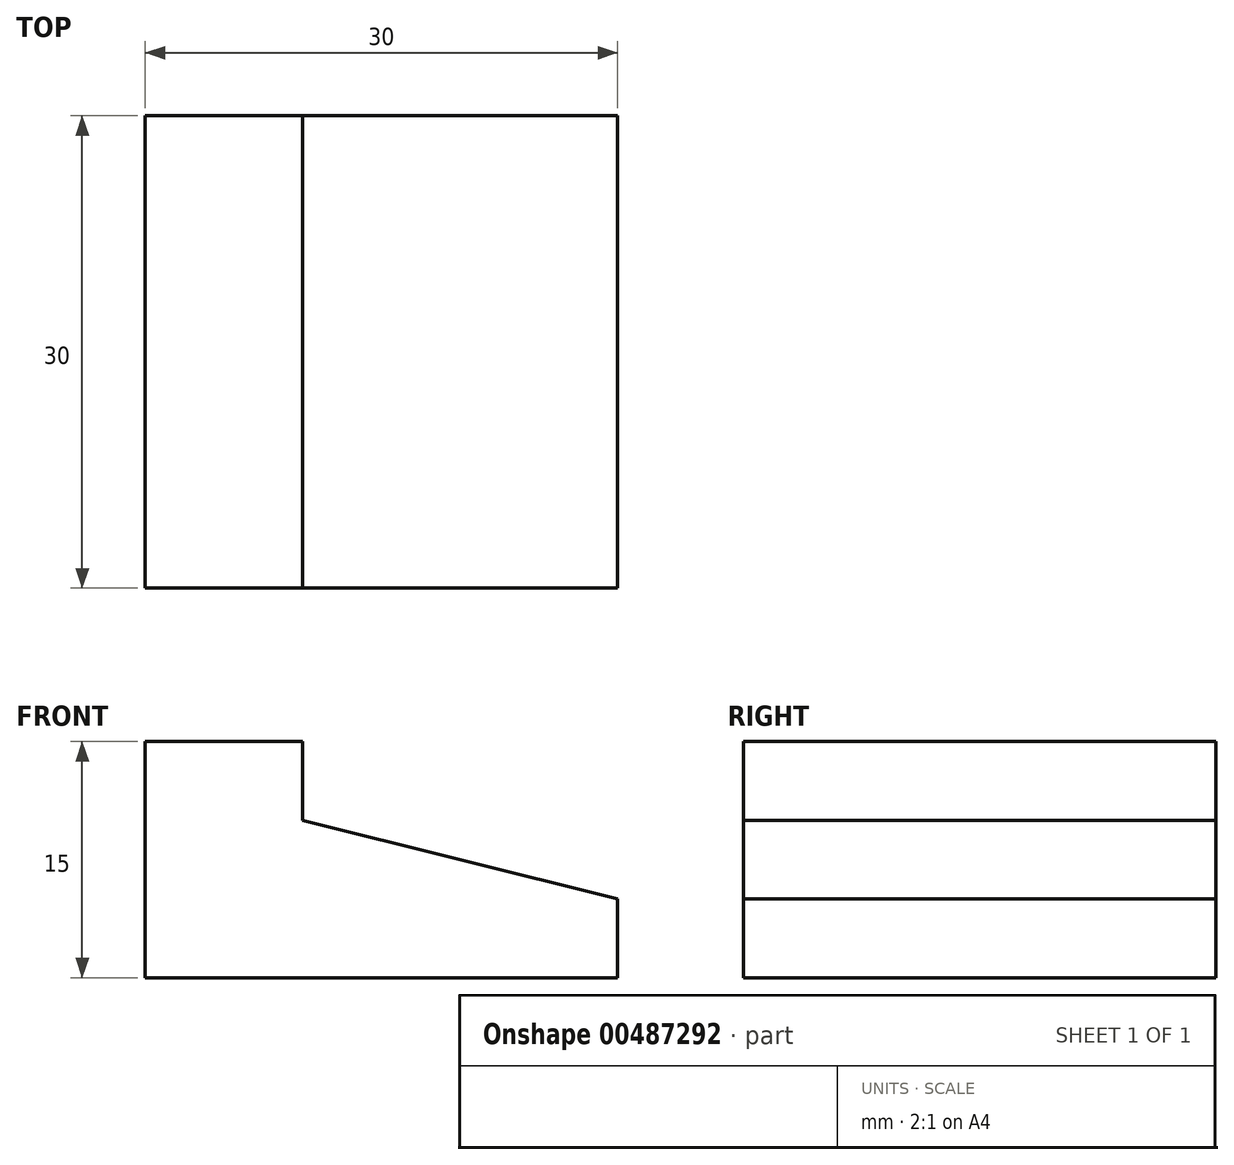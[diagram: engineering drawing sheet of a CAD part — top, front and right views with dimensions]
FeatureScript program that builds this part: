
annotation { "Feature Type Name" : "Feature", "Feature Type Description" : "" }
export const myFeature = defineFeature(function(context is Context, id is Id, definition is map)
    precondition{}
    {
        {
            var Q0;
            Q0=qCreatedBy(makeId("Top.planeOp"),FACE);
            var sketch = newSketch(context, id + "F0", { "sketchPlane" : qUnion([Q0])});
            skLineSegment(sketch, "E0.bottom", {"start": v(-45.49, 4.04) * mm, "end": v(-15.49, 4.04) * mm});
            skLineSegment(sketch, "E0.top", {"start": v(-45.49, -25.96) * mm, "end": v(-15.49, -25.96) * mm});
            skLineSegment(sketch, "E0.left", {"start": v(-45.49, 4.04) * mm, "end": v(-45.49, -25.96) * mm});
            skLineSegment(sketch, "E0.right", {"start": v(-15.49, 4.04) * mm, "end": v(-15.49, -25.96) * mm});
            skSolve(sketch);
        }
        {
            var Q0;
            Q0=makeQuery(id+"F0.imprint","IMPRINT",FACE,{"disambiguationData":[TD([[makeQuery(id+"F0.imprint","IMPRINT",EDGE,{"derivedFrom":sQuery(id+"F0.wireOp",EDGE,"E0.bottom")}),-1.0]])]});
            extrude(context, id + "F1", {"entities" : qUnion([Q0]), "depth" : 15 * mm});
        }
        {
            var Q0;
            Q0=makeQuery(id+"F1.opExtrude","SWEPT_FACE",FACE,{"disambiguationData":[OSD([sQuery(id+"F0.wireOp",EDGE,"E0.top")])]});
            var sketch = newSketch(context, id + "F2", { "sketchPlane" : qUnion([Q0])});
            skLineSegment(sketch, "E1", {"start": v(-15.49, 0) * mm, "end": v(-15.49, 5) * mm});
            skLineSegment(sketch, "E2", {"start": v(-15.49, 5) * mm, "end": v(-35.49, 10) * mm});
            skLineSegment(sketch, "E3", {"start": v(-35.49, 10) * mm, "end": v(-35.49, 15) * mm});
            skLineSegment(sketch, "E4", {"start": v(-35.49, 15) * mm, "end": v(-45.49, 15) * mm});
            skSolve(sketch);
        }
        {
            var Q0;
            {var subQ0=sQuery(id+"F2.wireOp",EDGE,"E2");Q0=makeQuery(id+"F2.imprint","IMPRINT",FACE,{"disambiguationData":[TD([[makeQuery(id+"F2.imprint","IMPRINT",EDGE,{"derivedFrom":subQ0}),-1.0]])]});}
            extrude(context, id + "F3", {"entities" : qUnion([Q0]), "operationType" : NewBodyOperationType.REMOVE, "endBound" : BoundingType.THROUGH_ALL, "oppositeDirection" : true, "depth" : 25 * mm});
        }
    });
